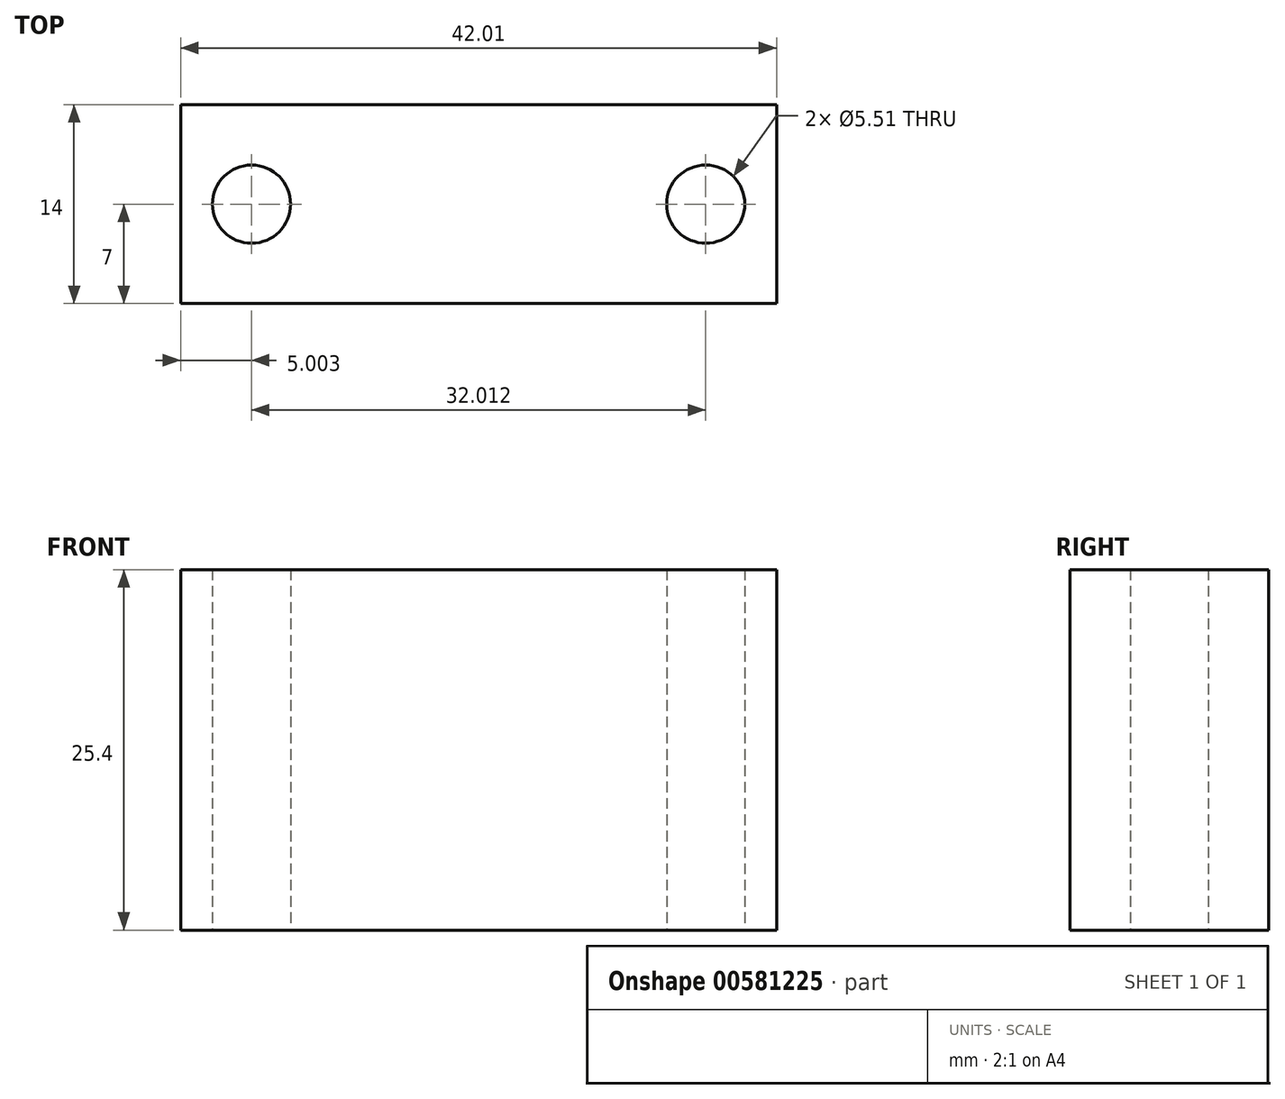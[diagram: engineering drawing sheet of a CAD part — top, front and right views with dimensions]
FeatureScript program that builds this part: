
annotation { "Feature Type Name" : "Feature", "Feature Type Description" : "" }
export const myFeature = defineFeature(function(context is Context, id is Id, definition is map)
    precondition{}
    {
        {
            var Q0;
            Q0=qCreatedBy(makeId("Top.planeOp"),FACE);
            var sketch = newSketch(context, id + "F0", { "sketchPlane" : qUnion([Q0])});
            skLineSegment(sketch, "E0.bottom", {"start": v(-158.76, 14.15) * mm, "end": v(-200.77, 14.15) * mm});
            skLineSegment(sketch, "E0.top", {"start": v(-158.76, 0.15) * mm, "end": v(-200.77, 0.15) * mm});
            skLineSegment(sketch, "E0.left", {"start": v(-158.76, 14.15) * mm, "end": v(-158.76, 0.15) * mm});
            skLineSegment(sketch, "E0.right", {"start": v(-200.77, 14.15) * mm, "end": v(-200.77, 0.15) * mm});
            skPoint(sketch, "E0.middle", {"position": v(-179.76, 7.15) * mm});
            skCircle(sketch, "E1", {"center": v(-163.76, 7.15) * mm, "radius": 2.76 * mm});
            skCircle(sketch, "E2.MirrorC", {"center": v(-195.77, 7.15) * mm, "radius": 2.76 * mm});
            skSolve(sketch);
        }
        {
            var Q0;
            Q0 = qSketchRegion(id + "F0", true);
            extrude(context, id + "F1", {"entities" : qUnion([Q0]), "depth" : 25.4 * mm, "offsetDistance" : 25.4 * mm});
        }
    });
